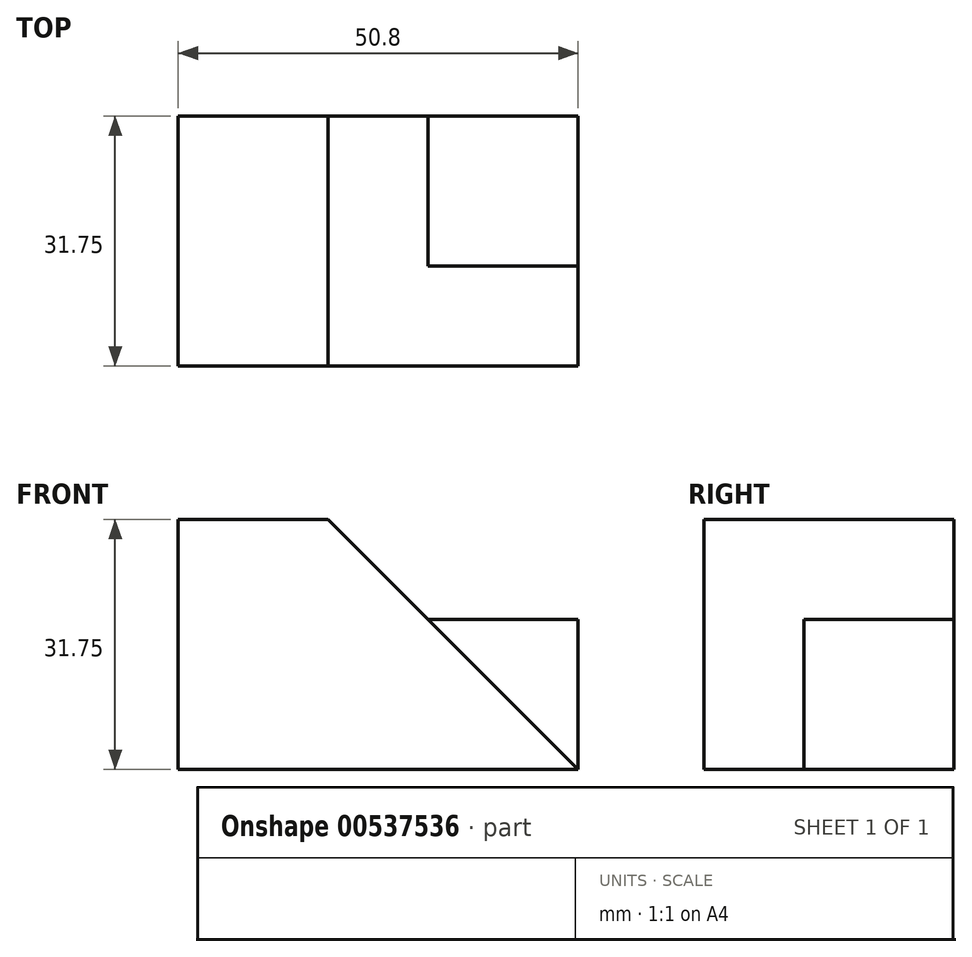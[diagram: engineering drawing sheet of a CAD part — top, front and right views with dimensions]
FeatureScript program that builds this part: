
annotation { "Feature Type Name" : "Feature", "Feature Type Description" : "" }
export const myFeature = defineFeature(function(context is Context, id is Id, definition is map)
    precondition{}
    {
        {
            var Q0;
            Q0=qCreatedBy(makeId("Front.planeOp"),FACE);
            var sketch = newSketch(context, id + "F0", { "sketchPlane" : qUnion([Q0])});
            skLineSegment(sketch, "E0", {"start": v(0, 0) * mm, "end": v(0, 31.75) * mm});
            skLineSegment(sketch, "E1", {"start": v(0, 31.75) * mm, "end": v(50.8, 31.75) * mm});
            skLineSegment(sketch, "E2", {"start": v(50.8, 31.75) * mm, "end": v(50.8, 0) * mm});
            skLineSegment(sketch, "E3", {"start": v(50.8, 0) * mm, "end": v(0, 0) * mm});
            skSolve(sketch);
        }
        {
            var Q0;
            Q0 = qSketchRegion(id + "F0", true);
            extrude(context, id + "F1", {"entities" : qUnion([Q0]), "depth" : 31.75 * mm, "offsetDistance" : 25.4 * mm});
        }
        {
            var Q0;
            Q0=makeQuery(id+"F1.opExtrude","CAP_FACE",FACE,{"disambiguationData":[OSD([sQuery(id+"F0.wireOp",EDGE,"E0"),sQuery(id+"F0.wireOp",EDGE,"E1"),sQuery(id+"F0.wireOp",EDGE,"E2"),sQuery(id+"F0.wireOp",EDGE,"E3")])],"isStart":false});
            var sketch = newSketch(context, id + "F2", { "sketchPlane" : qUnion([Q0])});
            skLineSegment(sketch, "E4", {"start": v(19.05, 31.75) * mm, "end": v(50.8, 0) * mm});
            skSolve(sketch);
        }
        {
            var Q0;
            {var subQ0=sQuery(id+"F2.wireOp",EDGE,"E4");Q0=makeQuery(id+"F2.imprint","IMPRINT",FACE,{"disambiguationData":[TD([[makeQuery(id+"F2.imprint","IMPRINT",EDGE,{"derivedFrom":subQ0}),1.0]])]});}
            extrude(context, id + "F3", {"entities" : qUnion([Q0]), "operationType" : NewBodyOperationType.REMOVE, "oppositeDirection" : true, "depth" : 12.7 * mm, "offsetDistance" : 25.4 * mm});
        }
        {
            var Q0;
            Q0=makeQuery(id+"F3.boolean.opBoolean","COPY",FACE,{"derivedFrom":makeQuery(id+"F3.opExtrude","CAP_FACE",FACE,{"disambiguationData":[OSD([sQuery(id+"F0.wireOp",EDGE,"E1"),sQuery(id+"F0.wireOp",EDGE,"E2"),sQuery(id+"F2.wireOp",EDGE,"E4")])],"isStart":false})});
            var sketch = newSketch(context, id + "F4", { "sketchPlane" : qUnion([Q0])});
            skLineSegment(sketch, "E5", {"start": v(50.8, 0) * mm, "end": v(50.8, 19.05) * mm});
            skLineSegment(sketch, "E6", {"start": v(50.8, 19.05) * mm, "end": v(31.75, 19.05) * mm});
            skSolve(sketch);
        }
        {
            var Q0;
            {var subQ0=sQuery(id+"F4.wireOp",EDGE,"E6");Q0=makeQuery(id+"F4.imprint","IMPRINT",FACE,{"disambiguationData":[TD([[makeQuery(id+"F4.imprint","IMPRINT",EDGE,{"derivedFrom":subQ0}),-1.0]])]});}
            extrude(context, id + "F5", {"entities" : qUnion([Q0]), "operationType" : NewBodyOperationType.REMOVE, "oppositeDirection" : true, "depth" : 19.05 * mm, "offsetDistance" : 25.4 * mm});
        }
    });
